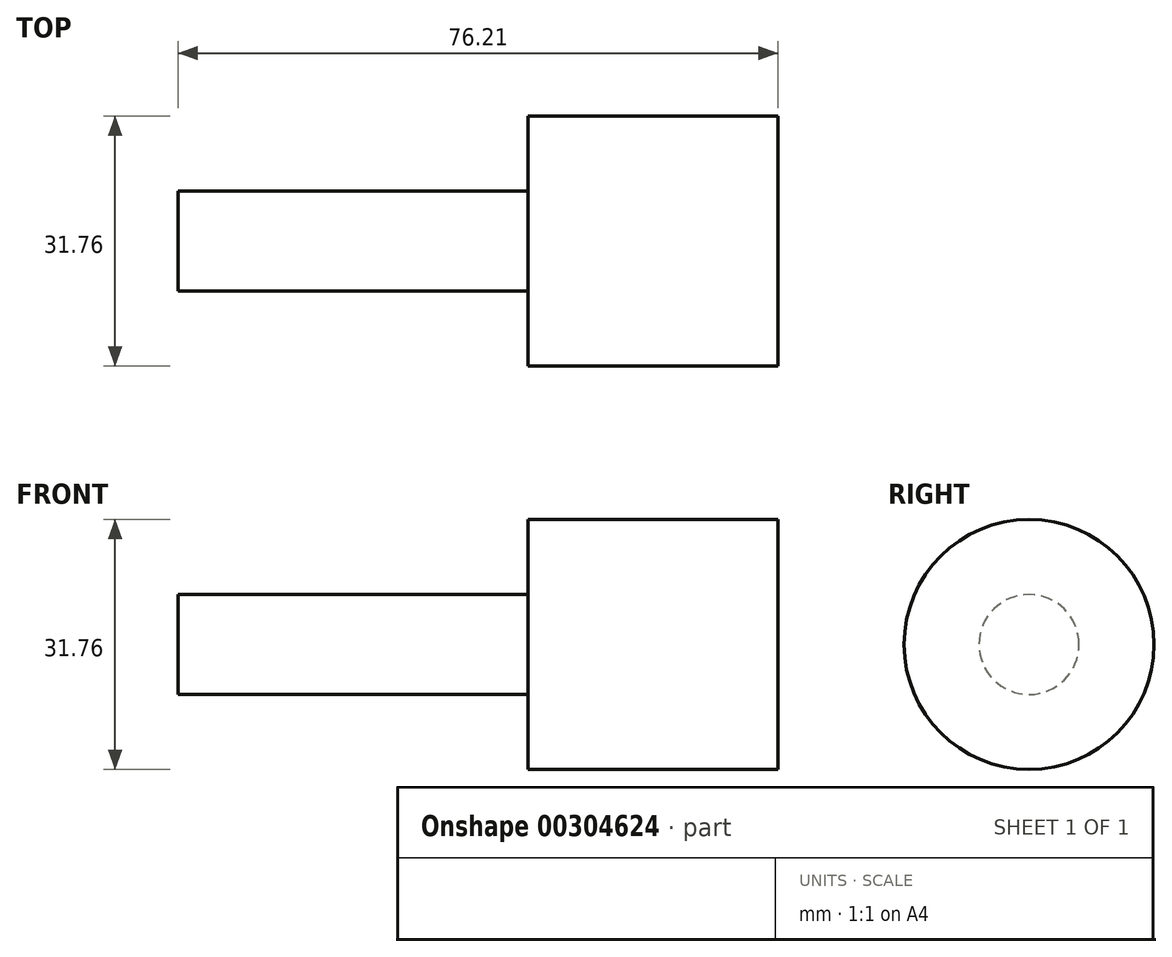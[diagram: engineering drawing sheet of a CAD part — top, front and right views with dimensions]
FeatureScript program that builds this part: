
annotation { "Feature Type Name" : "Feature", "Feature Type Description" : "" }
export const myFeature = defineFeature(function(context is Context, id is Id, definition is map)
    precondition{}
    {
        {
            var Q0;
            Q0=qCreatedBy(makeId("Right.planeOp"),FACE);
            var sketch = newSketch(context, id + "F0", { "sketchPlane" : qUnion([Q0])});
            skCircle(sketch, "E0", {"center": v(0, 0) * mm, "radius": 15.88 * mm});
            skSolve(sketch);
        }
        {
            var Q0;
            Q0=makeQuery(id+"F0.imprint","IMPRINT",FACE,{"disambiguationData":[TD([[makeQuery(id+"F0.imprint","IMPRINT",EDGE,{"derivedFrom":sQuery(id+"F0.wireOp",EDGE,"E0")}),1.0]])]});
            extrude(context, id + "F1", {"entities" : qUnion([Q0]), "endBound" : BoundingType.SYMMETRIC, "oppositeDirection" : true, "depth" : 31.75 * mm});
        }
        {
            var Q0;
            Q0=qCreatedBy(makeId("Front.planeOp"),FACE);
            var sketch = newSketch(context, id + "F2", { "sketchPlane" : qUnion([Q0])});
            skCircle(sketch, "E1", {"center": v(0, 0) * mm, "radius": 4.45 * mm});
            skSolve(sketch);
        }
        {
            var Q0;
            Q0=sQuery(id+"F2.wireOp",EDGE,"E1");
            extrude(context, id + "F3", {"bodyType" : ToolBodyType.SURFACE, "surfaceEntities" : qUnion([Q0]), "depth" : 76.2 * mm});
        }
        {
            var Q0;
            Q0=qCreatedBy(makeId("Front.planeOp"),FACE);
            var sketch = newSketch(context, id + "F4", { "sketchPlane" : qUnion([Q0])});
            skCircle(sketch, "E2", {"center": v(0, 0) * mm, "radius": 4.45 * mm});
            skSolve(sketch);
        }
        {
            var Q0;
            Q0=sQuery(id+"F4.wireOp",EDGE,"E2");
            extrude(context, id + "F5", {"bodyType" : ToolBodyType.SURFACE, "surfaceEntities" : qUnion([Q0]), "oppositeDirection" : true, "depth" : 76.2 * mm});
        }
        {
            var Q0;
            Q0=makeQuery(id+"F1.opExtrude","CAP_FACE",FACE,{"disambiguationData":[OSD([sQuery(id+"F0.wireOp",EDGE,"E0")])],"isStart":false});
            var sketch = newSketch(context, id + "F6", { "sketchPlane" : qUnion([Q0])});
            skCircle(sketch, "E3", {"center": v(0, 0) * mm, "radius": 6.35 * mm});
            skSolve(sketch);
        }
        {
            var Q0;
            Q0=makeQuery(id+"F6.imprint","IMPRINT",FACE,{"disambiguationData":[TD([[makeQuery(id+"F6.imprint","IMPRINT",EDGE,{"derivedFrom":sQuery(id+"F6.wireOp",EDGE,"E3")}),1.0]])]});
            extrude(context, id + "F7", {"entities" : qUnion([Q0]), "operationType" : NewBodyOperationType.ADD, "depth" : 44.45 * mm});
        }
    });
